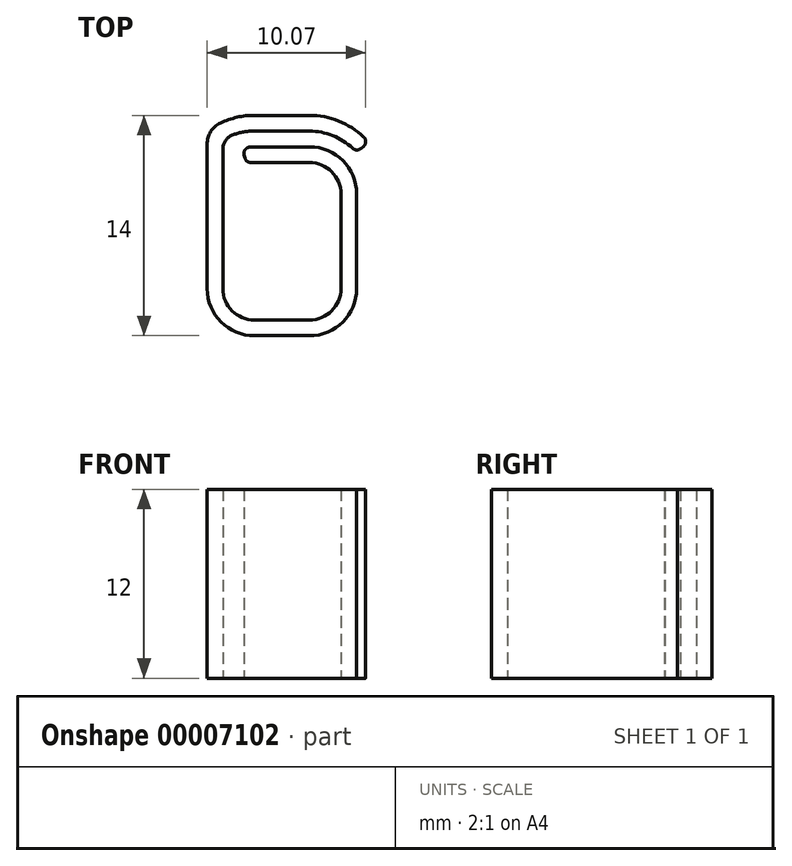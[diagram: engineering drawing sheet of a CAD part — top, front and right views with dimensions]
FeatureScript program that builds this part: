
annotation { "Feature Type Name" : "Feature", "Feature Type Description" : "" }
export const myFeature = defineFeature(function(context is Context, id is Id, definition is map)
    precondition{}
    {
        {
            var Q0;
            Q0=qCreatedBy(makeId("Top.planeOp"),FACE);
            var sketch = newSketch(context, id + "F0", { "sketchPlane" : qUnion([Q0])});
            skLineSegment(sketch, "E0.rect.bottom", {"start": v(1.75, 5) * mm, "end": v(-1.75, 5) * mm});
            skLineSegment(sketch, "E0.rect.top", {"start": v(1.75, -5) * mm, "end": v(-1.75, -5) * mm});
            skLineSegment(sketch, "E0.rect.left", {"start": v(3.75, 3) * mm, "end": v(3.75, -3) * mm});
            skLineSegment(sketch, "E0.rect.right", {"start": v(-3.75, 3) * mm, "end": v(-3.75, -3) * mm});
            skPoint(sketch, "E0.rect.middle", {"position": v(0, 0) * mm});
            skPoint(sketch, "E1.visualSharp", {"position": v(-3.75, 5) * mm});
            skArc(sketch, "E1.filletArc", {"start": v(-1.75, 5) * mm, "mid": v(-1.84, 5) * mm, "end": v(-1.92, 5) * mm});
            skPoint(sketch, "E2.visualSharp", {"position": v(3.75, 5) * mm});
            skArc(sketch, "E2.filletArc", {"start": v(3.75, 3) * mm, "mid": v(3.16, 4.41) * mm, "end": v(1.75, 5) * mm});
            skPoint(sketch, "E3.visualSharp", {"position": v(3.75, -5) * mm});
            skArc(sketch, "E3.filletArc", {"start": v(1.75, -5) * mm, "mid": v(3.16, -4.41) * mm, "end": v(3.75, -3) * mm});
            skPoint(sketch, "E4.visualSharp", {"position": v(-3.75, -5) * mm});
            skArc(sketch, "E4.filletArc", {"start": v(-3.75, -3) * mm, "mid": v(-3.16, -4.41) * mm, "end": v(-1.75, -5) * mm});
            skArc(sketch, "E5.0", {"start": v(4.75, 3) * mm, "mid": v(3.87, 5.12) * mm, "end": v(1.75, 6) * mm});
            skLineSegment(sketch, "E5.1", {"start": v(4.75, 3) * mm, "end": v(4.75, -3) * mm});
            skArc(sketch, "E5.2", {"start": v(1.75, -6) * mm, "mid": v(3.87, -5.12) * mm, "end": v(4.75, -3) * mm});
            skLineSegment(sketch, "E5.3", {"start": v(1.75, -6) * mm, "end": v(-1.75, -6) * mm});
            skArc(sketch, "E5.4", {"start": v(-4.75, -3) * mm, "mid": v(-3.87, -5.12) * mm, "end": v(-1.75, -6) * mm});
            skLineSegment(sketch, "E5.5", {"start": v(1.75, 6) * mm, "end": v(-1.75, 6) * mm});
            skLineSegment(sketch, "E5.6", {"start": v(-4.75, 3) * mm, "end": v(-4.75, -3) * mm});
            skArc(sketch, "E5.7", {"start": v(-1.75, 6) * mm, "mid": v(-1.9, 6) * mm, "end": v(-2.04, 5.99) * mm});
            skArc(sketch, "E6.0", {"start": v(-1.75, 7) * mm, "mid": v(-2.43, 6.94) * mm, "end": v(-3.08, 6.77) * mm});
            skLineSegment(sketch, "E6.1", {"start": v(1.75, 7) * mm, "end": v(-1.75, 7) * mm});
            skArc(sketch, "E6.2", {"start": v(4.5, 5.9) * mm, "mid": v(3.23, 6.72) * mm, "end": v(1.75, 7) * mm});
            skArc(sketch, "E7.0", {"start": v(-1.75, 8) * mm, "mid": v(-2.85, 7.88) * mm, "end": v(-3.9, 7.52) * mm});
            skLineSegment(sketch, "E7.1", {"start": v(1.75, 8) * mm, "end": v(-1.75, 8) * mm});
            skArc(sketch, "E7.2", {"start": v(5.2, 6.62) * mm, "mid": v(3.6, 7.64) * mm, "end": v(1.75, 8) * mm});
            skLineSegment(sketch, "E8", {"start": v(-3.75, 1.75) * mm, "end": v(-3.75, 5.83) * mm});
            skLineSegment(sketch, "E9", {"start": v(-4.75, 1.71) * mm, "end": v(-4.75, 6.16) * mm});
            skLineSegment(sketch, "E10", {"start": v(-2.34, 5.3) * mm, "end": v(-2.4, 5.49) * mm});
            skLineSegment(sketch, "E11", {"start": v(5.04, 5.9) * mm, "end": v(5.19, 6.03) * mm});
            skPoint(sketch, "E12.visualSharp", {"position": v(-4.75, 7) * mm});
            skArc(sketch, "E12.filletArc", {"start": v(-3.9, 7.52) * mm, "mid": v(-4.52, 6.96) * mm, "end": v(-4.75, 6.16) * mm});
            skPoint(sketch, "E13.visualSharp", {"position": v(-3.75, 6.46) * mm});
            skArc(sketch, "E13.filletArc", {"start": v(-3.08, 6.77) * mm, "mid": v(-3.57, 6.4) * mm, "end": v(-3.75, 5.83) * mm});
            skPoint(sketch, "E14.visualSharp", {"position": v(-2.5, 5.9) * mm});
            skArc(sketch, "E14.filletArc", {"start": v(-2.04, 5.99) * mm, "mid": v(-2.33, 5.82) * mm, "end": v(-2.4, 5.49) * mm});
            skPoint(sketch, "E15.visualSharp", {"position": v(-2.25, 4.94) * mm});
            skArc(sketch, "E15.filletArc", {"start": v(-2.34, 5.3) * mm, "mid": v(-2.19, 5.06) * mm, "end": v(-1.92, 5) * mm});
            skPoint(sketch, "E16.visualSharp", {"position": v(5.5, 6.3) * mm});
            skArc(sketch, "E16.filletArc", {"start": v(5.19, 6.03) * mm, "mid": v(5.32, 6.32) * mm, "end": v(5.2, 6.62) * mm});
            skPoint(sketch, "E17.visualSharp", {"position": v(4.75, 5.65) * mm});
            skArc(sketch, "E17.filletArc", {"start": v(4.5, 5.9) * mm, "mid": v(4.76, 5.8) * mm, "end": v(5.04, 5.9) * mm});
            skSolve(sketch);
        }
        {
            var Q0;
            Q0 = qSketchRegion(id + "F0", true);
            extrude(context, id + "F1", {"entities" : qUnion([Q0]), "depth" : 12 * mm});
        }
    });
